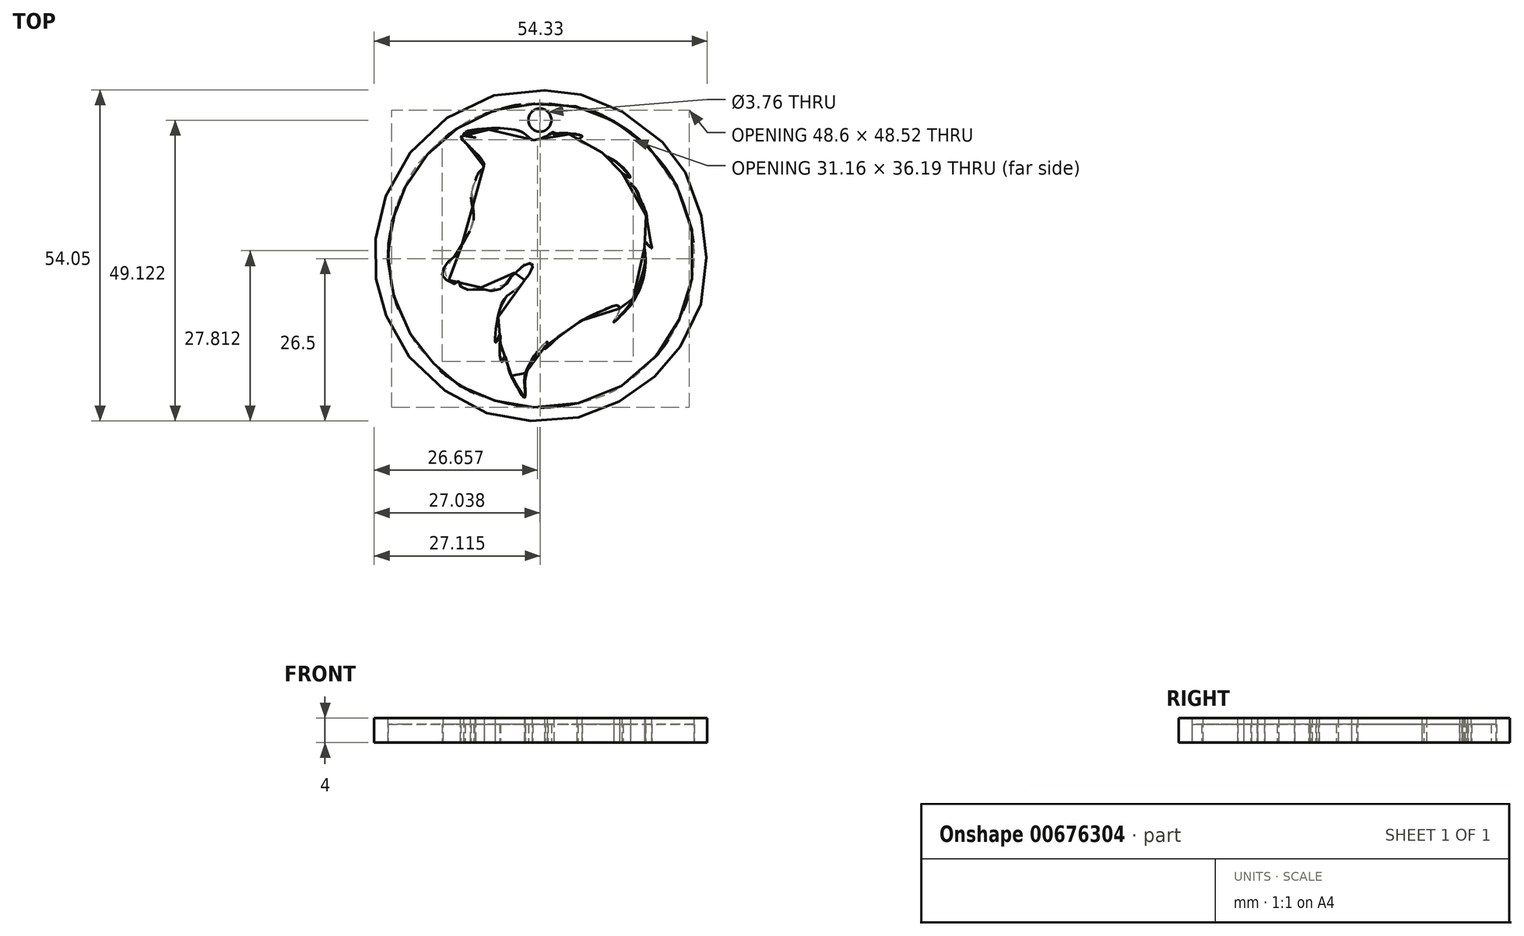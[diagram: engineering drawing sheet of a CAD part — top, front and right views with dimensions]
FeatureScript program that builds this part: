
annotation { "Feature Type Name" : "Feature", "Feature Type Description" : "" }
export const myFeature = defineFeature(function(context is Context, id is Id, definition is map)
    precondition{}
    {
        {
            var Q0;
            Q0=qCreatedBy(makeId("Top.planeOp"),FACE);
            var sketch = newSketch(context, id + "F0", { "sketchPlane" : qUnion([Q0])});
            skFitSpline(sketch, "E0", {"points": [v(18.56, 42.8) * mm, v(17.8, 41.54) * mm, v(17.05, 40.16) * mm, v(16.37, 38.1) * mm, v(17, 36.78) * mm, v(17.05, 34.78) * mm, v(16.5, 32.78) * mm, v(15.43, 30.46) * mm, v(13.74, 28.08) * mm, v(12.8, 26.96) * mm, v(11.92, 25.14) * mm, v(12.17, 24.64) * mm, v(14.11, 23.77) * mm, v(14.43, 24.14) * mm, v(14.93, 23.14) * mm, v(16.68, 22.64) * mm, v(18.62, 23.02) * mm, v(19.93, 22.58) * mm, v(22.06, 23.58) * mm, v(22.81, 24.64) * mm, v(24.31, 26.02) * mm, v(25.82, 27.27) * mm, v(26.44, 26.7) * mm, v(26, 25.02) * mm, v(24.88, 23.83) * mm, v(23.5, 22.45) * mm, v(21.87, 20.89) * mm, v(20.93, 18.26) * mm, v(20.5, 15.44) * mm, v(20.56, 14.07) * mm, v(21.12, 15.26) * mm, v(21.31, 12.56) * mm, v(21.62, 10.88) * mm, v(22, 11.81) * mm, v(22.69, 9.62) * mm, v(23.69, 7.56) * mm, v(25.25, 5.18) * mm, v(25.2, 7.37) * mm, v(25.57, 9.56) * mm, v(27.13, 12.25) * mm, v(28.45, 13.7) * mm, v(28.95, 14.13) * mm, v(28.5, 13.13) * mm, v(30.07, 14.57) * mm, v(31.7, 15.82) * mm, v(34.45, 17.57) * mm, v(36.46, 18.76) * mm, v(38.15, 19.45) * mm, v(40.53, 20.14) * mm, v(40.59, 19.07) * mm, v(39.77, 17.57) * mm, v(41.4, 18.95) * mm, v(42.6, 20.64) * mm, v(43.6, 22.45) * mm, v(44.28, 24.7) * mm, v(44.9, 27.46) * mm, v(44.97, 30.46) * mm, v(45.85, 29.46) * mm, v(45.6, 31.65) * mm, v(44.9, 35.28) * mm, v(44.1, 37.28) * mm, v(42.97, 39.54) * mm, v(41.15, 41.66) * mm, v(42.47, 40.91) * mm, v(40.71, 42.98) * mm, v(38.46, 44.6) * mm, v(36.46, 45.92) * mm, v(33.77, 47.3) * mm, v(34.58, 47.67) * mm, v(32.08, 47.99) * mm, v(30.01, 47.92) * mm, v(30.01, 48.36) * mm, v(28.82, 47.73) * mm, v(27, 47.1) * mm, v(26.38, 47.1) * mm, v(25.2, 47.99) * mm, v(22.37, 48.86) * mm, v(18.37, 48.67) * mm, v(15.3, 47.99) * mm, v(17.24, 47.48) * mm, v(14.74, 47.6) * mm, v(15.43, 46.92) * mm, v(16.93, 45.42) * mm, v(18.43, 43.8) * mm, v(18.56, 42.8) * mm]});
            skSolve(sketch);
        }
        {
            var Q0;
            Q0=qCreatedBy(makeId("Top.planeOp"),FACE);
            var sketch = newSketch(context, id + "F1", { "sketchPlane" : qUnion([Q0])});
            skFitSpline(sketch, "E1", {"points": [v(20.34, 51.97) * mm, v(16.77, 50.4) * mm, v(13.27, 48.32) * mm, v(10.74, 46.1) * mm, v(7.83, 42.96) * mm, v(6.05, 39.99) * mm, v(4.63, 36.94) * mm, v(3.67, 34.18) * mm, v(3.07, 30.46) * mm, v(2.92, 27.34) * mm, v(3.3, 24.14) * mm, v(4.11, 20.94) * mm, v(5.75, 17.07) * mm, v(7.6, 13.8) * mm, v(9.77, 11.34) * mm, v(11.4, 9.48) * mm, v(13.5, 7.69) * mm, v(16.47, 5.98) * mm, v(19.67, 4.79) * mm, v(23.02, 3.82) * mm, v(26.66, 3.45) * mm, v(30.83, 3.52) * mm, v(36.56, 4.86) * mm, v(40.73, 6.72) * mm, v(44.97, 10.15) * mm, v(47.73, 12.97) * mm, v(49.96, 16.7) * mm, v(51.67, 20.56) * mm, v(52.64, 24.95) * mm, v(52.8, 30.69) * mm, v(51.6, 35.97) * mm, v(49.44, 40.8) * mm, v(46.46, 44.9) * mm, v(42.82, 48.4) * mm, v(39.4, 50.4) * mm, v(36.2, 51.9) * mm, v(31.58, 52.86) * mm, v(27.78, 53.01) * mm, v(23.69, 52.79) * mm, v(20.34, 51.97) * mm]});
            skFitSpline(sketch, "E2", {"points": [v(34.48, 54.5) * mm, v(38.42, 53.09) * mm, v(41.77, 51.37) * mm, v(46.39, 48.1) * mm, v(48.77, 45.5) * mm, v(50.33, 43.49) * mm, v(52.2, 40.36) * mm, v(53.6, 36.27) * mm, v(54.73, 32.02) * mm, v(54.87, 28.75) * mm, v(55.02, 25.62) * mm, v(54.13, 20.56) * mm, v(51.97, 15.58) * mm, v(50.33, 12.82) * mm, v(48.25, 10.15) * mm, v(46.1, 8.14) * mm, v(43.04, 5.83) * mm, v(39.76, 3.9) * mm, v(35.9, 2.33) * mm, v(32.7, 1.59) * mm, v(27.48, 1.21) * mm, v(24.28, 1.36) * mm, v(19.97, 2.26) * mm, v(15.65, 3.97) * mm, v(11.78, 6.5) * mm, v(7.68, 10.07) * mm, v(5.45, 13.2) * mm, v(3, 17.51) * mm, v(2.1, 20.2) * mm, v(1.28, 22.95) * mm, v(0.76, 26.44) * mm, v(0.76, 29.72) * mm, v(1.2, 32.4) * mm, v(2.1, 36.42) * mm, v(3.81, 40.88) * mm, v(6.72, 45.2) * mm, v(10.36, 49) * mm, v(14.16, 51.75) * mm, v(19.3, 54.13) * mm, v(25.85, 55.24) * mm, v(29.12, 55.17) * mm, v(32.17, 55.02) * mm, v(34.48, 54.5) * mm]});
            skSolve(sketch);
        }
        {
            var Q0;
            Q0=qCreatedBy(makeId("Top.planeOp"),FACE);
            var sketch = newSketch(context, id + "F2", { "sketchPlane" : qUnion([Q0])});
            skFitSpline(sketch, "E3", {"points": [v(5.97, 40.06) * mm, v(4.63, 37.23) * mm, v(3.81, 33.89) * mm, v(3.07, 30.39) * mm, v(3.07, 27.26) * mm, v(3.44, 24.14) * mm, v(4.19, 20.79) * mm, v(5.67, 17.22) * mm, v(7.54, 13.8) * mm, v(9.62, 11.48) * mm, v(11.4, 9.48) * mm, v(13.56, 7.84) * mm, v(16.4, 6.05) * mm, v(19.37, 4.86) * mm, v(22.94, 3.97) * mm, v(26.44, 3.45) * mm, v(30.76, 3.6) * mm, v(36.71, 4.86) * mm, v(40.88, 6.8) * mm, v(45.05, 10.15) * mm, v(47.73, 13.05) * mm, v(50.04, 16.7) * mm, v(51.6, 20.42) * mm, v(52.64, 24.43) * mm, v(52.8, 30.61) * mm, v(51.52, 35.67) * mm, v(49.52, 40.58) * mm, v(46.46, 44.68) * mm, v(42.9, 48.1) * mm, v(39.32, 50.33) * mm, v(36.34, 51.82) * mm, v(31.65, 52.71) * mm, v(27.78, 53.09) * mm, v(23.54, 52.71) * mm, v(20.56, 51.9) * mm, v(16.7, 50.48) * mm, v(13.12, 48.17) * mm, v(10.74, 46.24) * mm, v(7.68, 42.96) * mm, v(5.97, 40.06) * mm]});
            skFitSpline(sketch, "E4", {"points": [v(18.33, 43.78) * mm, v(18.63, 42.67) * mm, v(17.8, 41.85) * mm, v(17.06, 40.06) * mm, v(16.47, 38.28) * mm, v(16.91, 34.93) * mm, v(16.47, 32.62) * mm, v(15.2, 30.31) * mm, v(13.71, 28) * mm, v(12.45, 26.89) * mm, v(11.78, 25.25) * mm, v(12.15, 24.5) * mm, v(14.01, 23.62) * mm, v(14.46, 24.06) * mm, v(14.76, 23.17) * mm, v(16.7, 22.57) * mm, v(18.55, 22.72) * mm, v(19.97, 22.42) * mm, v(22.05, 23.32) * mm, v(22.94, 24.58) * mm, v(24.43, 26) * mm, v(25.92, 26.96) * mm, v(26.6, 26.67) * mm, v(25.92, 25.1) * mm, v(24.8, 23.69) * mm, v(23.46, 22.42) * mm, v(21.9, 21.09) * mm, v(20.86, 18.1) * mm, v(20.49, 15.35) * mm, v(20.56, 14.02) * mm, v(21.23, 15.2) * mm, v(21.16, 12.68) * mm, v(21.6, 10.89) * mm, v(22.05, 11.86) * mm, v(22.65, 9.7) * mm, v(23.69, 7.32) * mm, v(25.25, 5.01) * mm, v(25.32, 7.32) * mm, v(25.77, 9.62) * mm, v(27.04, 12) * mm, v(28.3, 13.72) * mm, v(29.05, 14.02) * mm, v(28.6, 12.97) * mm, v(30.01, 14.24) * mm, v(31.87, 15.73) * mm, v(34.33, 17.44) * mm, v(36.42, 18.55) * mm, v(38.42, 19.45) * mm, v(40.43, 20.04) * mm, v(40.66, 19.15) * mm, v(39.76, 17.29) * mm, v(41.4, 18.85) * mm, v(42.67, 20.27) * mm, v(43.86, 22.35) * mm, v(44.97, 27.34) * mm, v(44.97, 30.24) * mm, v(45.94, 29.42) * mm, v(45.5, 31.73) * mm, v(45.05, 35.22) * mm, v(44.08, 37.53) * mm, v(43.19, 39.4) * mm, v(41.33, 41.25) * mm, v(42.44, 40.96) * mm, v(40.88, 42.96) * mm, v(38.42, 44.6) * mm, v(36.49, 45.8) * mm, v(33.96, 47.13) * mm, v(34.63, 47.65) * mm, v(32.4, 48.17) * mm, v(30.39, 48.17) * mm, v(30.09, 48.17) * mm, v(28.9, 47.58) * mm, v(27.11, 47.06) * mm, v(26.52, 47.06) * mm, v(25.18, 48.17) * mm, v(22.65, 48.92) * mm, v(18.33, 48.92) * mm, v(15.57, 48.17) * mm, v(17.06, 47.43) * mm, v(14.9, 47.5) * mm, v(15.35, 46.83) * mm, v(16.99, 45.27) * mm, v(18.33, 43.78) * mm]});
            skCircle(sketch, "E5", {"center": v(27.74, 50.33) * mm, "radius": 1.88 * mm});
            skSolve(sketch);
        }
        {
            var Q0;
            Q0=qCreatedBy(makeId("Top.planeOp"),FACE);
            var sketch = newSketch(context, id + "F3", { "sketchPlane" : qUnion([Q0])});
            skFitSpline(sketch, "E6", {"points": [v(20.72, 34.65) * mm, v(22.17, 35.37) * mm, v(23.26, 36.76) * mm, v(23.32, 38.88) * mm, v(23.86, 38.51) * mm, v(24.04, 40.08) * mm, v(24.4, 41.65) * mm, v(24.95, 41.95) * mm, v(26.4, 40.38) * mm, v(27, 39.24) * mm, v(28.15, 40.75) * mm, v(29.24, 42.2) * mm, v(30.99, 43.04) * mm, v(32.56, 42.07) * mm, v(34.25, 40.02) * mm, v(35.51, 37.24) * mm, v(36.36, 35.25) * mm, v(35.27, 35.68) * mm, v(35.4, 33.08) * mm, v(35.33, 30.48) * mm, v(34.43, 27.22) * mm, v(33.04, 24.8) * mm, v(31.29, 23.36) * mm, v(29.78, 21.37) * mm, v(31.47, 21.85) * mm, v(30.8, 20.16) * mm, v(29.78, 17.2) * mm, v(28.7, 13.94) * mm, v(29.3, 14) * mm, v(29.84, 15.7) * mm, v(30.62, 18.35) * mm, v(31.23, 19.98) * mm, v(32.07, 21.18) * mm, v(32.56, 22.63) * mm, v(31.6, 22.33) * mm, v(33.82, 24.87) * mm, v(35.21, 27.64) * mm, v(36, 31.33) * mm, v(35.7, 35.13) * mm, v(36.66, 33.8) * mm, v(36.54, 33.86) * mm, v(36.66, 33.86) * mm, v(36.78, 36.28) * mm, v(35.45, 39.72) * mm, v(33.28, 43.1) * mm, v(34.13, 42.98) * mm, v(32.2, 43.77) * mm, v(31.17, 43.65) * mm, v(31.1, 44.61) * mm, v(30.32, 43.7) * mm, v(29.54, 43.34) * mm, v(28.33, 42.14) * mm, v(27.48, 40.26) * mm, v(27.79, 44) * mm, v(27.18, 47.03) * mm, v(26.52, 47.15) * mm, v(26.94, 46) * mm, v(27.24, 44.19) * mm, v(27, 41.47) * mm, v(27.06, 40.26) * mm, v(25.92, 41.71) * mm, v(24.47, 42.74) * mm, v(22.78, 44.61) * mm, v(20.24, 46.3) * mm, v(15.6, 47.93) * mm, v(16.07, 47.45) * mm, v(18.8, 46.54) * mm, v(21.45, 44.85) * mm, v(24.1, 42.32) * mm, v(23.5, 41.35) * mm, v(23.38, 39.3) * mm, v(21.57, 41.53) * mm, v(18.55, 43.34) * mm, v(18.49, 42.74) * mm, v(20.72, 41.65) * mm, v(22.47, 39.18) * mm, v(21.63, 39.18) * mm, v(20.36, 37.9) * mm, v(19.7, 36.04) * mm, v(20, 34.77) * mm, v(19.76, 33.2) * mm, v(19.58, 31.09) * mm, v(19.82, 29.27) * mm, v(18.6, 28.67) * mm, v(16.68, 27.7) * mm, v(14.26, 25.95) * mm, v(14.08, 23.96) * mm, v(14.62, 24.08) * mm, v(14.93, 25.4) * mm, v(17.1, 27.22) * mm, v(19.64, 28.19) * mm, v(20.72, 28.67) * mm, v(20.54, 29.7) * mm, v(20.48, 31.75) * mm, v(20.48, 33.68) * mm, v(20.72, 34.65) * mm]});
            skSolve(sketch);
        }
        {
            var Q0;
            Q0=makeQuery(id+"F0.imprint","IMPRINT",FACE,{"disambiguationData":[TD([[makeQuery(id+"F0.imprint","IMPRINT",EDGE,{"derivedFrom":sQuery(id+"F0.wireOp",EDGE,"E0")}),1.0]])]});
            extrude(context, id + "F4", {"entities" : qUnion([Q0]), "depth" : 4 * mm, "offsetDistance" : 25 * mm});
        }
        {
            var Q0;
            Q0=makeQuery(id+"F1.imprint","IMPRINT",FACE,{"disambiguationData":[TD([[makeQuery(id+"F1.imprint","IMPRINT",EDGE,{"derivedFrom":sQuery(id+"F1.wireOp",EDGE,"E1")}),-1.0]])]});
            extrude(context, id + "F5", {"entities" : qUnion([Q0]), "depth" : 4 * mm, "offsetDistance" : 25 * mm});
        }
        {
            var Q0;
            Q0=makeQuery(id+"F2.imprint","IMPRINT",FACE,{"disambiguationData":[TD([[makeQuery(id+"F2.imprint","IMPRINT",EDGE,{"derivedFrom":sQuery(id+"F2.wireOp",EDGE,"E3")}),1.0]])]});
            extrude(context, id + "F6", {"entities" : qUnion([Q0]), "depth" : 3 * mm, "offsetDistance" : 25 * mm});
        }
        {
            var Q0;
            Q0=sQuery(id+"F3.wireOp",EDGE,"E6");
            extrude(context, id + "F7", {"bodyType" : ToolBodyType.SURFACE, "surfaceEntities" : qUnion([Q0]), "depth" : 2 * mm, "offsetDistance" : 25 * mm});
        }
        {
            var Q0;
            Q0=makeQuery(id+"F6.opExtrude","CAP_FACE",FACE,{"disambiguationData":[OSD([sQuery(id+"F2.wireOp",EDGE,"E3"),sQuery(id+"F2.wireOp",EDGE,"E4")])],"isStart":false});
            var sketch = newSketch(context, id + "F8", { "sketchPlane" : qUnion([Q0])});
            skCircle(sketch, "E7", {"center": v(26.69, 51.19) * mm, "radius": 1.58 * mm});
            skSolve(sketch);
        }
        {
            var Q0;
            Q0 = qSketchRegion(id + "F8", true);
            extrude(context, id + "F9", {"entities" : qUnion([Q0]), "operationType" : NewBodyOperationType.ADD, "depth" : 4 * mm, "offsetDistance" : 25 * mm});
        }
        {
            var Q0;
            Q0=makeQuery(id+"F9.opExtrude","CAP_FACE",FACE,{"disambiguationData":[OSD([sQuery(id+"F8.wireOp",EDGE,"E7")])],"isStart":false});
            extrude(context, id + "F10", {"entities" : qUnion([Q0]), "operationType" : NewBodyOperationType.REMOVE, "oppositeDirection" : true, "depth" : 4 * mm, "offsetDistance" : 25 * mm});
        }
    });
